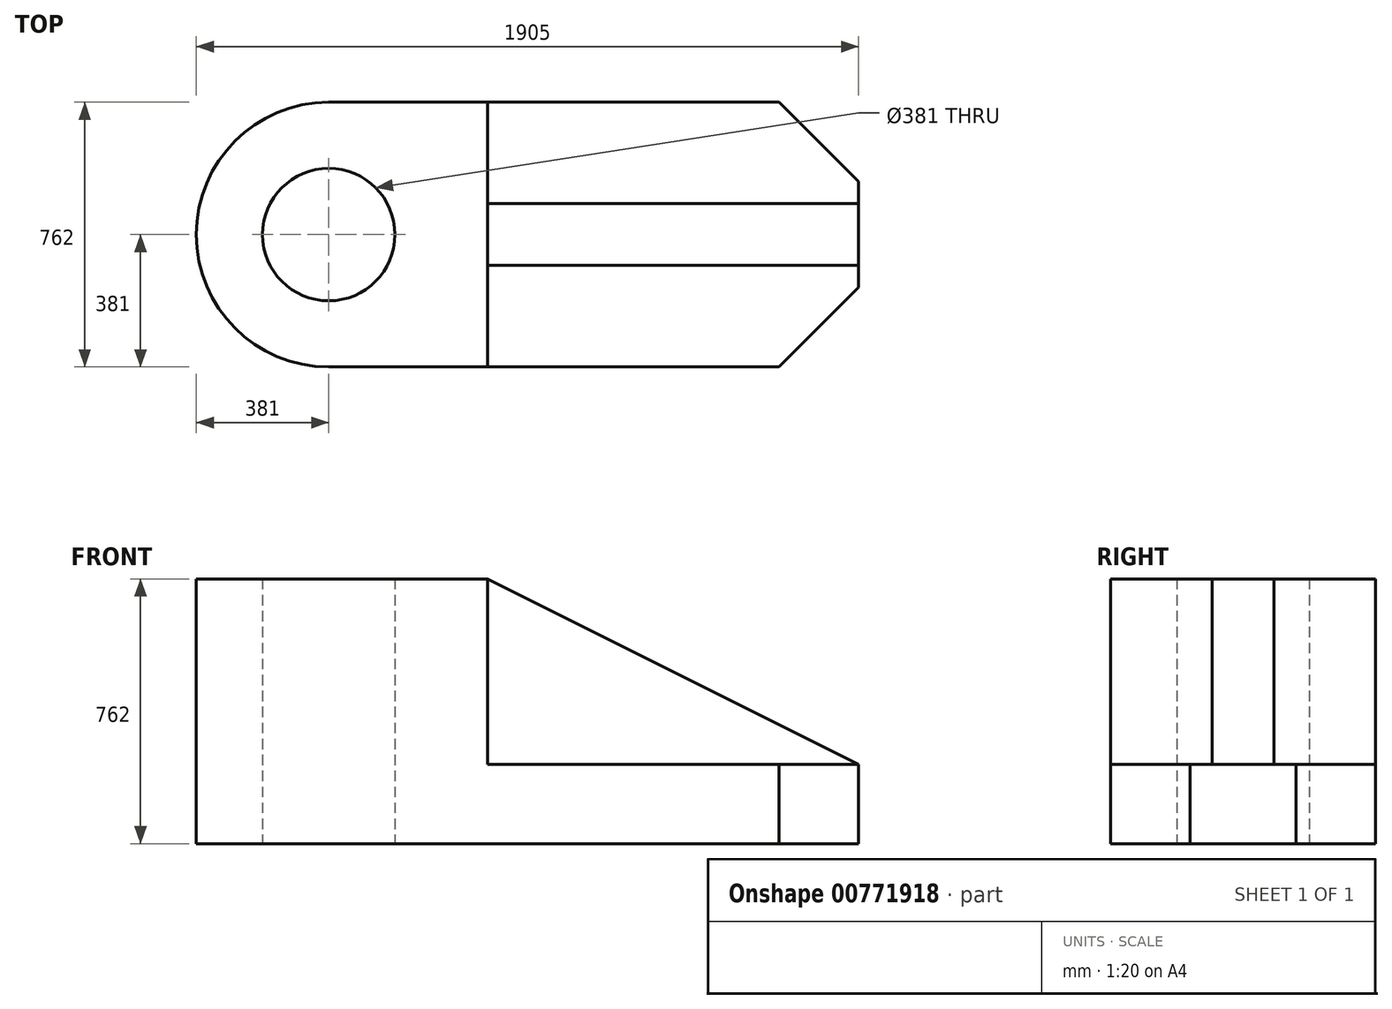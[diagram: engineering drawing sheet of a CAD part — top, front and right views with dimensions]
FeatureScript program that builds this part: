
annotation { "Feature Type Name" : "Feature", "Feature Type Description" : "" }
export const myFeature = defineFeature(function(context is Context, id is Id, definition is map)
    precondition{}
    {
        {
            var Q0;
            Q0=qCreatedBy(makeId("Top.planeOp"),FACE);
            var sketch = newSketch(context, id + "F0", { "sketchPlane" : qUnion([Q0])});
            skLineSegment(sketch, "E0", {"start": v(0, -381) * mm, "end": v(457.2, -381) * mm});
            skLineSegment(sketch, "E1", {"start": v(457.2, -381) * mm, "end": v(457.2, 381) * mm});
            skLineSegment(sketch, "E2", {"start": v(457.2, 381) * mm, "end": v(0, 381) * mm});
            skCircle(sketch, "E3", {"center": v(0, 0) * mm, "radius": 381 * mm});
            skCircle(sketch, "E4", {"center": v(0, 0) * mm, "radius": 190.5 * mm});
            skSolve(sketch);
        }
        {
            var Q0;
            Q0=makeQuery(id+"F0.imprint","IMPRINT",FACE,{"disambiguationData":[TD([[makeQuery(id+"F0.imprint","IMPRINT",EDGE,{"derivedFrom":sQuery(id+"F0.wireOp",EDGE,"E4")}),-1.0]])]});
            var Q1;
            {var subQ0=sQuery(id+"F0.wireOp",EDGE,"E0");Q1=makeQuery(id+"F0.imprint","IMPRINT",FACE,{"disambiguationData":[TD([[makeQuery(id+"F0.imprint","IMPRINT",EDGE,{"derivedFrom":subQ0}),1.0]])]});}
            extrude(context, id + "F1", {"entities" : qUnion([Q0, Q1]), "depth" : 762 * mm, "offsetDistance" : 25.4 * mm});
        }
        {
            var Q0;
            Q0=makeQuery(id+"F1.opExtrude","SWEPT_FACE",FACE,{"disambiguationData":[OSD([sQuery(id+"F0.wireOp",EDGE,"E1")])]});
            var sketch = newSketch(context, id + "F2", { "sketchPlane" : qUnion([Q0])});
            skLineSegment(sketch, "E5", {"start": v(-381, 0) * mm, "end": v(-381, 228.6) * mm});
            skLineSegment(sketch, "E6", {"start": v(-381, 228.6) * mm, "end": v(381, 228.6) * mm});
            skLineSegment(sketch, "E7", {"start": v(381, 228.6) * mm, "end": v(381, 0) * mm});
            skLineSegment(sketch, "E8", {"start": v(381, 0) * mm, "end": v(-381, 0) * mm});
            skSolve(sketch);
        }
        {
            var Q0;
            Q0=makeQuery(id+"F2.imprint","IMPRINT",FACE,{"disambiguationData":[TD([[makeQuery(id+"F2.imprint","IMPRINT",EDGE,{"derivedFrom":sQuery(id+"F2.wireOp",EDGE,"E5")}),1.0]])]});
            extrude(context, id + "F3", {"entities" : qUnion([Q0]), "operationType" : NewBodyOperationType.ADD, "depth" : 1066.8 * mm, "offsetDistance" : 25.4 * mm});
        }
        {
            var Q0;
            Q0=makeQuery(id+"F3.opExtrude","SWEPT_FACE",FACE,{"disambiguationData":[OSD([sQuery(id+"F2.wireOp",EDGE,"E6")])]});
            var sketch = newSketch(context, id + "F4", { "sketchPlane" : qUnion([Q0])});
            skLineSegment(sketch, "E9", {"start": v(1524, -381) * mm, "end": v(1295.4, -381) * mm});
            skLineSegment(sketch, "E10", {"start": v(1524, -381) * mm, "end": v(1524, -152.4) * mm});
            skLineSegment(sketch, "E11", {"start": v(1524, -152.4) * mm, "end": v(1295.4, -381) * mm});
            skLineSegment(sketch, "E12", {"start": v(1524, 381) * mm, "end": v(1295.4, 381) * mm});
            skLineSegment(sketch, "E13", {"start": v(1524, 381) * mm, "end": v(1524, 152.4) * mm});
            skLineSegment(sketch, "E14", {"start": v(1524, 152.4) * mm, "end": v(1295.4, 381) * mm});
            skSolve(sketch);
        }
        {
            var Q0;
            Q0=makeQuery(id+"F4.imprint","IMPRINT",FACE,{"disambiguationData":[TD([[makeQuery(id+"F4.imprint","IMPRINT",EDGE,{"derivedFrom":sQuery(id+"F4.wireOp",EDGE,"E12")}),1.0]])]});
            var Q1;
            Q1=makeQuery(id+"F4.imprint","IMPRINT",FACE,{"disambiguationData":[TD([[makeQuery(id+"F4.imprint","IMPRINT",EDGE,{"derivedFrom":sQuery(id+"F4.wireOp",EDGE,"E9")}),-1.0]])]});
            extrude(context, id + "F5", {"entities" : qUnion([Q0, Q1]), "operationType" : NewBodyOperationType.REMOVE, "endBound" : BoundingType.THROUGH_ALL, "oppositeDirection" : true, "depth" : 25.4 * mm, "offsetDistance" : 25.4 * mm});
        }
        {
            var Q0;
            Q0=makeQuery(id+"F1.opExtrude","SWEPT_FACE",FACE,{"disambiguationData":[OSD([sQuery(id+"F0.wireOp",EDGE,"E1")])]});
            var sketch = newSketch(context, id + "F6", { "sketchPlane" : qUnion([Q0])});
            skLineSegment(sketch, "E15", {"start": v(-88.9, 228.6) * mm, "end": v(88.9, 228.6) * mm});
            skLineSegment(sketch, "E16", {"start": v(-88.9, 228.6) * mm, "end": v(-88.9, 762) * mm});
            skLineSegment(sketch, "E17", {"start": v(-88.9, 762) * mm, "end": v(88.9, 762) * mm});
            skLineSegment(sketch, "E18", {"start": v(88.9, 762) * mm, "end": v(88.9, 228.6) * mm});
            skSolve(sketch);
        }
        {
            var Q0;
            Q0=makeQuery(id+"F6.imprint","IMPRINT",FACE,{"disambiguationData":[TD([[makeQuery(id+"F6.imprint","IMPRINT",EDGE,{"derivedFrom":sQuery(id+"F6.wireOp",EDGE,"E15")}),1.0]])]});
            extrude(context, id + "F7", {"entities" : qUnion([Q0]), "operationType" : NewBodyOperationType.ADD, "depth" : 1066.8 * mm, "offsetDistance" : 25.4 * mm});
        }
        {
            var Q0;
            Q0=makeQuery(id+"F7.opExtrude","SWEPT_FACE",FACE,{"disambiguationData":[OSD([sQuery(id+"F6.wireOp",EDGE,"E16")])]});
            var sketch = newSketch(context, id + "F8", { "sketchPlane" : qUnion([Q0])});
            skLineSegment(sketch, "E19", {"start": v(457.2, 762) * mm, "end": v(1524, 228.6) * mm});
            skLineSegment(sketch, "E20", {"start": v(1524, 228.6) * mm, "end": v(1524, 762) * mm});
            skLineSegment(sketch, "E21", {"start": v(1524, 762) * mm, "end": v(457.2, 762) * mm});
            skSolve(sketch);
        }
        {
            var Q0;
            Q0=makeQuery(id+"F8.imprint","IMPRINT",FACE,{"disambiguationData":[TD([[makeQuery(id+"F8.imprint","IMPRINT",EDGE,{"derivedFrom":sQuery(id+"F8.wireOp",EDGE,"E19")}),1.0]])]});
            extrude(context, id + "F9", {"entities" : qUnion([Q0]), "operationType" : NewBodyOperationType.REMOVE, "endBound" : BoundingType.THROUGH_ALL, "oppositeDirection" : true, "depth" : 25.4 * mm, "offsetDistance" : 25.4 * mm});
        }
    });
